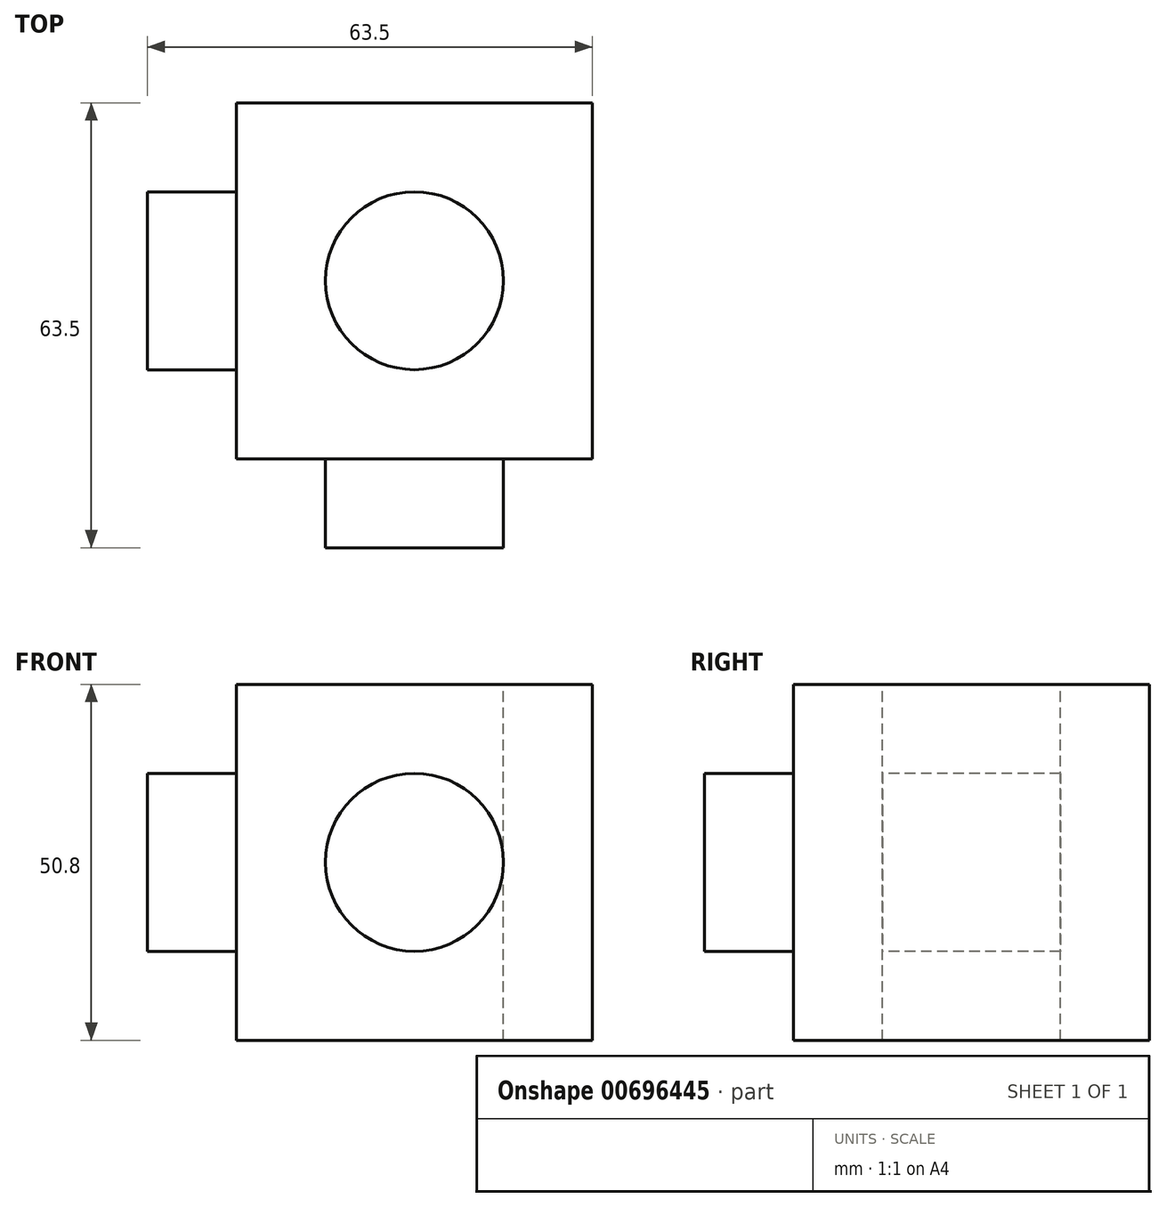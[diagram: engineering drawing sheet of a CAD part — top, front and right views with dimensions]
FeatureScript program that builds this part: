
annotation { "Feature Type Name" : "Feature", "Feature Type Description" : "" }
export const myFeature = defineFeature(function(context is Context, id is Id, definition is map)
    precondition{}
    {
        {
            var Q0;
            Q0=qCreatedBy(makeId("Top.planeOp"),FACE);
            var sketch = newSketch(context, id + "F0", { "sketchPlane" : qUnion([Q0])});
            skLineSegment(sketch, "E0.bottom", {"start": v(0, 0) * mm, "end": v(-50.8, 0) * mm});
            skLineSegment(sketch, "E0.top", {"start": v(0, 50.8) * mm, "end": v(-50.8, 50.8) * mm});
            skLineSegment(sketch, "E0.left", {"start": v(0, 0) * mm, "end": v(0, 50.8) * mm});
            skLineSegment(sketch, "E0.right", {"start": v(-50.8, 0) * mm, "end": v(-50.8, 50.8) * mm});
            skSolve(sketch);
        }
        {
            var Q0;
            Q0 = qSketchRegion(id + "F0", true);
            extrude(context, id + "F1", {"entities" : qUnion([Q0]), "depth" : 50.8 * mm, "offsetDistance" : 25.4 * mm});
        }
        {
            var Q0;
            Q0=makeQuery(id+"F1.opExtrude","CAP_FACE",FACE,{"disambiguationData":[OSD([sQuery(id+"F0.wireOp",EDGE,"E0.bottom"),sQuery(id+"F0.wireOp",EDGE,"E0.top"),sQuery(id+"F0.wireOp",EDGE,"E0.left"),sQuery(id+"F0.wireOp",EDGE,"E0.right")])],"isStart":false});
            var sketch = newSketch(context, id + "F2", { "sketchPlane" : qUnion([Q0])});
            skCircle(sketch, "E1", {"center": v(-25.4, 25.4) * mm, "radius": 12.7 * mm});
            skSolve(sketch);
        }
        {
            var Q0;
            Q0 = qSketchRegion(id + "F2", true);
            extrude(context, id + "F3", {"entities" : qUnion([Q0]), "operationType" : NewBodyOperationType.REMOVE, "oppositeDirection" : true, "depth" : 50.8 * mm, "offsetDistance" : 25.4 * mm});
        }
        {
            var Q0;
            Q0=makeQuery(id+"F1.opExtrude","SWEPT_FACE",FACE,{"disambiguationData":[OSD([sQuery(id+"F0.wireOp",EDGE,"E0.right")])]});
            var sketch = newSketch(context, id + "F4", { "sketchPlane" : qUnion([Q0])});
            skLineSegment(sketch, "E2.bottom", {"start": v(-38.1, 38.1) * mm, "end": v(-12.7, 38.1) * mm});
            skLineSegment(sketch, "E2.top", {"start": v(-38.1, 12.7) * mm, "end": v(-12.7, 12.7) * mm});
            skLineSegment(sketch, "E2.left", {"start": v(-38.1, 38.1) * mm, "end": v(-38.1, 12.7) * mm});
            skLineSegment(sketch, "E2.right", {"start": v(-12.7, 38.1) * mm, "end": v(-12.7, 12.7) * mm});
            skSolve(sketch);
        }
        {
            var Q0;
            Q0 = qSketchRegion(id + "F4", true);
            extrude(context, id + "F5", {"entities" : qUnion([Q0]), "operationType" : NewBodyOperationType.ADD, "depth" : 12.7 * mm, "offsetDistance" : 25.4 * mm});
        }
        {
            var Q0;
            Q0=makeQuery(id+"F1.opExtrude","SWEPT_FACE",FACE,{"disambiguationData":[OSD([sQuery(id+"F0.wireOp",EDGE,"E0.bottom")])]});
            var sketch = newSketch(context, id + "F6", { "sketchPlane" : qUnion([Q0])});
            skCircle(sketch, "E3", {"center": v(-25.4, 25.4) * mm, "radius": 12.7 * mm});
            skSolve(sketch);
        }
        {
            var Q0;
            Q0 = qSketchRegion(id + "F6", true);
            extrude(context, id + "F7", {"entities" : qUnion([Q0]), "operationType" : NewBodyOperationType.ADD, "depth" : 12.7 * mm, "offsetDistance" : 25.4 * mm});
        }
    });
